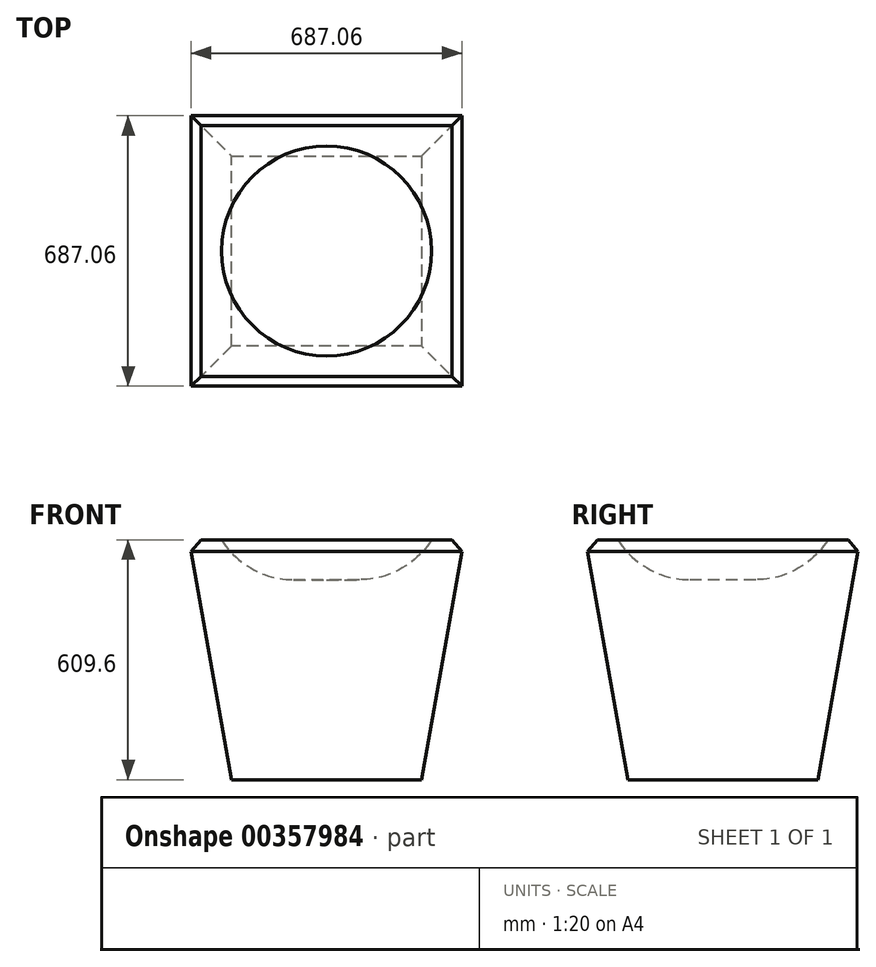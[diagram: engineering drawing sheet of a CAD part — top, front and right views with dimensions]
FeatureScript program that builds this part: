
annotation { "Feature Type Name" : "Feature", "Feature Type Description" : "" }
export const myFeature = defineFeature(function(context is Context, id is Id, definition is map)
    precondition{}
    {
        {
            var Q0;
            Q0=qCreatedBy(makeId("Top.planeOp"),FACE);
            var sketch = newSketch(context, id + "F0", { "sketchPlane" : qUnion([Q0])});
            skLineSegment(sketch, "E0.bottom", {"start": v(241.3, 241.3) * mm, "end": v(-241.3, 241.3) * mm});
            skLineSegment(sketch, "E0.top", {"start": v(241.3, -241.3) * mm, "end": v(-241.3, -241.3) * mm});
            skLineSegment(sketch, "E0.left", {"start": v(241.3, 241.3) * mm, "end": v(241.3, -241.3) * mm});
            skLineSegment(sketch, "E0.right", {"start": v(-241.3, 241.3) * mm, "end": v(-241.3, -241.3) * mm});
            skPoint(sketch, "E0.middle", {"position": v(0, 0) * mm});
            skSolve(sketch);
        }
        {
            var Q0;
            Q0 = qSketchRegion(id + "F0", true);
            extrude(context, id + "F1", {"entities" : qUnion([Q0]), "depth" : 609.6 * mm, "hasDraft" : true, "draftAngle" : 10 * degree, "offsetDistance" : 25.4 * mm});
        }
        {
            var Q0;
            Q0=makeQuery(id+"F1.opExtrude","CAP_FACE",FACE,{"disambiguationData":[OSD([sQuery(id+"F0.wireOp",EDGE,"E0.bottom"),sQuery(id+"F0.wireOp",EDGE,"E0.top"),sQuery(id+"F0.wireOp",EDGE,"E0.left"),sQuery(id+"F0.wireOp",EDGE,"E0.right")])],"isStart":false});
            chamfer(context, id + "F2", {"entities" : qUnion([Q0]), "width" : 25.4 * mm, "tangentPropagation" : true});
        }
        {
            var Q0;
            {var subQ0=sQuery(id+"F0.wireOp",EDGE,"E0.right");Q0=makeQuery(id+"F2.opChamfer","BLEND_EDGE",EDGE,{"blendedFrom":[makeQuery(id+"F1.opExtrude","CAP_EDGE",EDGE,{"disambiguationData":[OSD([subQ0])],"isStart":false}),makeQuery(id+"F1.opExtrude","CAP_FACE",FACE,{"disambiguationData":[OSD([sQuery(id+"F0.wireOp",EDGE,"E0.bottom"),sQuery(id+"F0.wireOp",EDGE,"E0.top"),sQuery(id+"F0.wireOp",EDGE,"E0.left"),subQ0])],"isStart":false})],"blendedInto":[makeQuery(id+"F1.opExtrude","CAP_FACE",FACE,{"disambiguationData":[OSD([sQuery(id+"F0.wireOp",EDGE,"E0.bottom"),sQuery(id+"F0.wireOp",EDGE,"E0.top"),sQuery(id+"F0.wireOp",EDGE,"E0.left"),subQ0])],"isStart":false})]});}
            cPoint(context, id + "F3", {"entities" : qUnion([Q0]), "parameter" : 0.5});
        }
        {
            var Q0;
            {var subQ0=sQuery(id+"F0.wireOp",EDGE,"E0.right");Q0=makeQuery(id+"F2.opChamfer","BLEND_EDGE",EDGE,{"blendedFrom":[makeQuery(id+"F1.opExtrude","CAP_EDGE",EDGE,{"disambiguationData":[OSD([subQ0])],"isStart":false}),makeQuery(id+"F1.opExtrude","SWEPT_FACE",FACE,{"disambiguationData":[OSD([subQ0])]})],"blendedInto":[makeQuery(id+"F1.opExtrude","SWEPT_FACE",FACE,{"disambiguationData":[OSD([subQ0])]})]});}
            cPoint(context, id + "F4", {"entities" : qUnion([Q0]), "parameter" : 0.5});
        }
        {
            var Q0;
            Q0=makeQuery(id+"F1.opExtrude","CAP_EDGE",EDGE,{"disambiguationData":[OSD([sQuery(id+"F0.wireOp",EDGE,"E0.right")])],"isStart":true});
            cPoint(context, id + "F5", {"entities" : qUnion([Q0]), "parameter" : 0.5});
        }
        {
            var Q0;
            Q0 = qCreatedBy(id + "F3" ,VERTEX);
            var Q1;
            Q1 = qCreatedBy(id + "F4" ,VERTEX);
            var Q2;
            Q2 = qCreatedBy(id + "F5" ,VERTEX);
            cPlane(context, id + "F6", {"entities" : qUnion([Q0, Q1, Q2]), "cplaneType" : CPlaneType.THREE_POINT, "offset" : 25.4 * mm, "width" : 152.4 * mm, "height" : 152.4 * mm});
        }
        {
            var Q0;
            Q0=qCreatedBy(id+"F6.planeOp",FACE);
            var sketch = newSketch(context, id + "F7", { "sketchPlane" : qUnion([Q0])});
            skLineSegment(sketch, "E1", {"start": v(0, 695.8) * mm, "end": v(0, 196.14) * mm, "construction": true});
            skLineSegment(sketch, "E2", {"start": v(0, 508) * mm, "end": v(-83.47, 508) * mm});
            skLineSegment(sketch, "E3.1", {"start": v(0, 609.6) * mm, "end": v(-266.7, 609.6) * mm});
            skArc(sketch, "E4", {"start": v(-83.47, 508) * mm, "mid": v(-188.23, 535.1) * mm, "end": v(-266.7, 609.6) * mm});
            skLineSegment(sketch, "E5", {"start": v(0, 609.6) * mm, "end": v(0, 508) * mm});
            skSolve(sketch);
        }
        {
            var Q0;
            Q0 = qSketchRegion(id + "F7", true);
            var Q1;
            Q1=sQuery(id+"F7.wireOp",EDGE,"E1");
            revolve(context, id + "F8", {"operationType" : NewBodyOperationType.REMOVE, "entities" : qUnion([Q0]), "axis" : qUnion([Q1]), "revolveType" : RevolveType.FULL, "oppositeDirection" : true});
        }
    });
